# Revit family: AM 1000 S1S2 TB
name_source: partatom
category: Mechanical Equipment
units: mm (PartAtom-declared; Revit-internal decimal feet)

## family parameters
Always vertical = Yes
Cut with Voids When Loaded = No
OmniClass Number = 23.75.00.00
OmniClass Title = Climate Control (HVAC)
Part Type = Normal
Room Calculation Point = No
Round Connector Dimension = Use Diameter
Shared = No
Work Plane-Based = No

## types (1)
- AM 1000 S1S2 TB
    BMS IN = (PTS) 2x2x0,6
    BMS Out = (PTS) 2x2x0,6
    BMS Panel = (PTS) 2x2x0,6
    Buttom Panel = Yes
    Condensate = 9 mm  [stored 0.0295276 ft]
    Condensate conector = Ø6/9 mm
    Electrical connection = 1  ~ 230V+N+PE / 3 ~ 230/400V+N+PE/ 50 Hz
    Exhaust Air = 315 mm
    L-C Duct ESupply = 237 mm
    Manufacturer = Airmaster A/S
    Max. flow rate 30 dB(A) with ePM10 50% filters = 950 m³
    Max. flow rate 30 dB(A) with ePM10 55% filters = 926 m³
    Max. flow rate 30 dB(A) with ePM10 80% filters = 903 m³
    Max. flow rate 35 dB(A) with ePM10 50% filters = 1050 m³
    Max. flow rate 35 dB(A) with ePM10 55% filters = 1025 m³
    Max. flow rate 35 dB(A) with ePM10 80% filters = 998 m³
    Model = AM 1000 S1S2 TB
    Network Conection = AWG 24 CAT 5e STP
    Nominal current, air handling unit = 2,2 A
    Nominal current, electrical comfort heating surface = 6,5 A
    Nominal current, electrical preheating surface = 10 A
    Phase 1 - Max Current = 19 A
    Phase 1 - Max Power Consumption = 4105 W
    R-C Duct Exhaust = 318 mm
    Suply Air In = 315 mm
    T-C Duct Exhaust = 258 mm
    T-C Duct Supply = 258 mm
    Total Depth = 1248 mm  [stored 4.09449 ft]
    Total Hight = 560 mm  [stored 1.83727 ft]
    Total Width = 2325 mm
    URL = www.airmaster-as.com
    Water Heater Surface IN = 15 mm  [stored 0.0492126 ft]
    Water Heater Surface Return = 15 mm  [stored 0.0492126 ft]
    Water heating surface Return = 1/2" (DN 15)
    Water heating surface in = 1/2" (DN 15)
    Weight (Standard Unit) = 301.5

note: [stored X ft] marks values corroborated as IEEE doubles in the binary element streams (Revit-internal decimal feet)

## geometry (parser evidence)
native form markers: Sweep x7
no freeform markers — native parametric forms only
